# Revit family: 3-721-xx - 37-721-xx - Eris (Outdoor)
name_source: partatom
category: Lighting Fixtures
revit_build: Autodesk Revit 2018 (Build: 20180423_1000(x64)
units: mm (PartAtom-declared; Revit-internal decimal feet)

## family parameters
Cut with Voids When Loaded = No
Host = Face
Light Source = Yes
Part Type = Normal
Room Calculation Point = No
Round Connector Dimension = Use Diameter
Shared = No

## types (2) — shared parameters
Color Filter = 16777215
Diffuser = White Opal Glass
Dimming Lamp Color Temperature Shift = <None>
Emit Shape Visible in Rendering = No
Emit from Rectangle Length = 30 "
Emit from Rectangle Width = 10 "
Lamp = LED Array
Manufacturer = Oxygen Lighting
Model = 3-721-xx / 37-721-xx - Name
Other = <By Category>
Photometric Web File = 3-721 Eris Outdoor.ies
Tilt Angle = 180.00°
URL = www.oxygenlighting.com
Wattage Comments = 20.00 W at 120 V
zero-valued in all types: Default Elevation

## per-type parameters (varying)
| type | Metal Finish |
| 3-721-16 / 37-721-16 - Eris | 16 - Gray |
| 3-721-22 / 37-721-22 - Eris | 22- Oiled Bronze |

## geometry (parser evidence)
native form markers: Extrusion x1, Sweep x7
no freeform markers — native parametric forms only
